# Revit family: Ovoid_Chair_BIM
name_source: partatom
category: Arredi
units: mm (PartAtom-declared; Revit-internal decimal feet)

## family parameters
Attiva taglio nelle viste = No
Basato su piano di lavoro = No
Condiviso = No
Numero OmniClass = 23.40.20.00
Origine composizione di rendering = Geometria famiglia
Punto di calcolo locali = No
Sempre verticale = Sì
Taglio con vuoti quando caricato = No
Titolo OmniClass = General Furniture and Specialties

## types (1)
- CB-61
    AVAILABLE FINISHES = Ebonized black lacquer on Oak (EB). Raw effect lacquer on Oak (RE). Hand rubbed natural oil on Oak or Walnut (NA), or hand rubbed black oil on Walnut (BO).
    BASE MATERIAL = BASSAM_FELLOWS_OAK_O-NA
    BIM BADGE = https://bim.archiproducts.com
    COLLECTION = Ovoid
    DEPTH = 570 mm  [stored 1.87008 ft]
    Descrizione = Upholstered solid wood chair
    HEIGHT = 756 mm  [stored 2.48031 ft]
    MATERIAL DESCRIPTION = Solid wood frame. Foam upholstery with welt detail.
    Modello = Ovoid Chair
    PILLOW MATERIAL = BASSAM_FELLOWS_ELEGANT_LEATHER_48027_OLIVE
    PRODUCT CODE = CB-61
    PRODUCT SHEET = https://www.archiproducts.com
    Produttore = BassamFellows
    Prospetto di default = 0 mm  [stored 0 ft]
    TECHNICAL SHEET = https://bassamfellows.com
    UPHOLSTERY MATERIAL = BASSAM_FELLOWS_COMFORT_LEATHER_43632_CAMEL
    URL = https://bassamfellows.com
    WIDTH = 492 mm  [stored 1.61417 ft]

note: [stored X ft] marks values corroborated as IEEE doubles in the binary element streams (Revit-internal decimal feet)

## geometry (parser evidence)
native form markers: Sweep x3
no freeform markers — native parametric forms only
